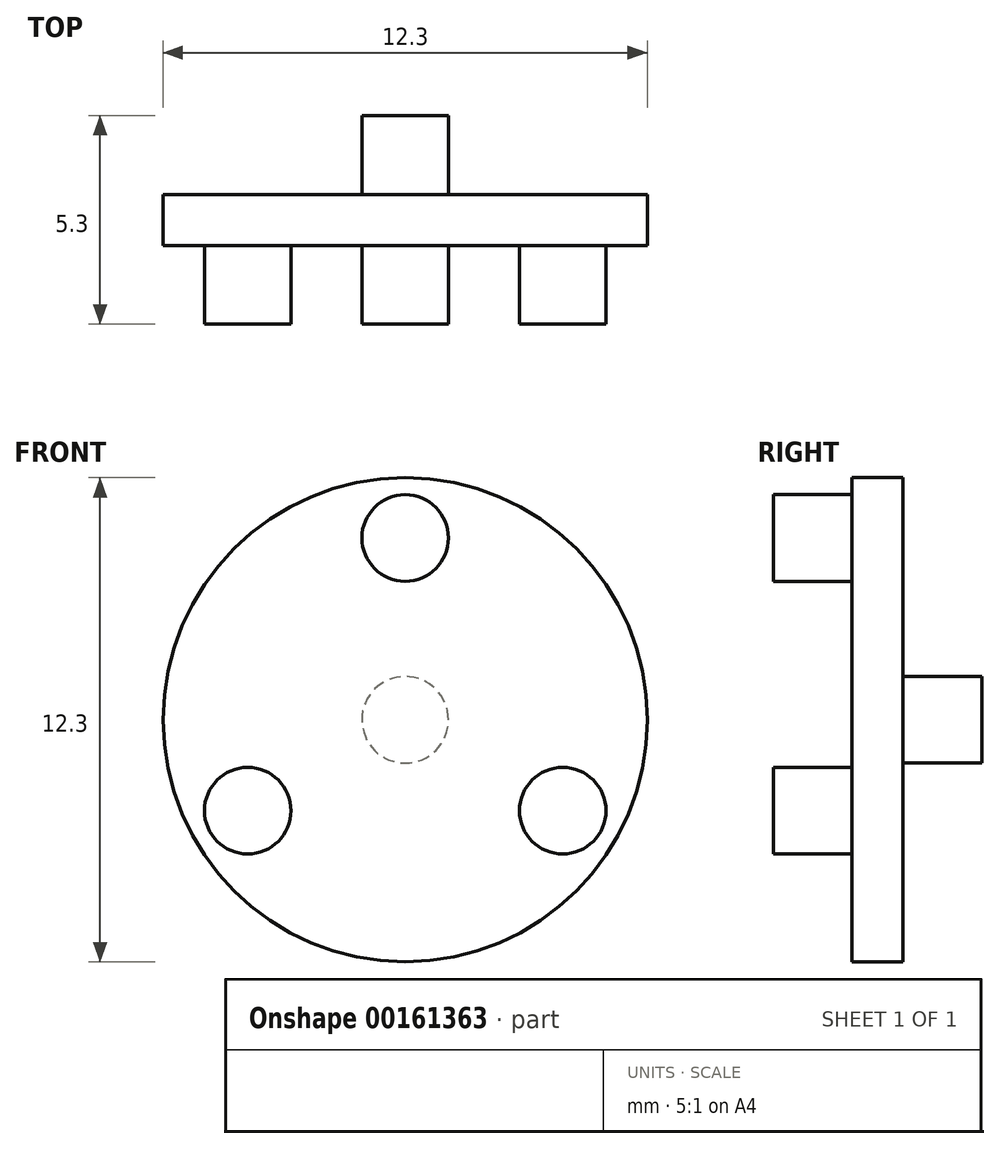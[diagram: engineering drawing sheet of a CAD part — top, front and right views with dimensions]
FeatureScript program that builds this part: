
annotation { "Feature Type Name" : "Feature", "Feature Type Description" : "" }
export const myFeature = defineFeature(function(context is Context, id is Id, definition is map)
    precondition{}
    {
        {
            var Q0;
            Q0=qCreatedBy(makeId("Front.planeOp"),FACE);
            var sketch = newSketch(context, id + "F0", { "sketchPlane" : qUnion([Q0])});
            skCircle(sketch, "E0", {"center": v(0, 0) * mm, "radius": 6.15 * mm});
            skSolve(sketch);
        }
        {
            var Q0;
            Q0=qSketchRegion(id+"F0",true);
            extrude(context, id + "F1", {"entities" : qUnion([Q0]), "depth" : 1.3 * mm});
        }
        {
            var Q0;
            Q0=makeQuery(id+"F1.opExtrude","CAP_FACE",FACE,{"disambiguationData":[OSD([sQuery(id+"F0.wireOp",EDGE,"E0")])],"isStart":false});
            var sketch = newSketch(context, id + "F2", { "sketchPlane" : qUnion([Q0])});
            skCircle(sketch, "E1", {"center": v(0, 0) * mm, "radius": 4.62 * mm, "construction": true});
            skLineSegment(sketch, "E2", {"start": v(0, 6.15) * mm, "end": v(0, -6.15) * mm, "construction": true});
            skLineSegment(sketch, "E3", {"start": v(-6.15, 0) * mm, "end": v(6.15, 0) * mm, "construction": true});
            skCircle(sketch, "E4", {"center": v(0, 4.62) * mm, "radius": 1.1 * mm});
            skCircle(sketch, "E5.1.0", {"center": v(-4, -2.3) * mm, "radius": 1.1 * mm});
            skCircle(sketch, "E5.2.0", {"center": v(4, -2.3) * mm, "radius": 1.1 * mm});
            skSolve(sketch);
        }
        {
            var Q0;
            Q0=qSketchRegion(id+"F2",true);
            extrude(context, id + "F3", {"entities" : qUnion([Q0]), "operationType" : NewBodyOperationType.ADD, "depth" : 2 * mm});
        }
        {
            var Q0;
            Q0=makeQuery(id+"F1.opExtrude","CAP_FACE",FACE,{"disambiguationData":[OSD([sQuery(id+"F0.wireOp",EDGE,"E0")])],"isStart":true});
            var Q1;
            Q1=makeQuery(id+"F1.opExtrude","CAP_FACE",FACE,{"disambiguationData":[OSD([sQuery(id+"F0.wireOp",EDGE,"E0")])],"isStart":true});
            var sketch = newSketch(context, id + "F4", { "sketchPlane" : qUnion([Q0, Q1])});
            skCircle(sketch, "E6", {"center": v(0, 0) * mm, "radius": 1.1 * mm});
            skSolve(sketch);
        }
        {
            var Q0;
            Q0=qSketchRegion(id+"F4",true);
            extrude(context, id + "F5", {"entities" : qUnion([Q0]), "operationType" : NewBodyOperationType.ADD, "depth" : 2 * mm});
        }
    });
